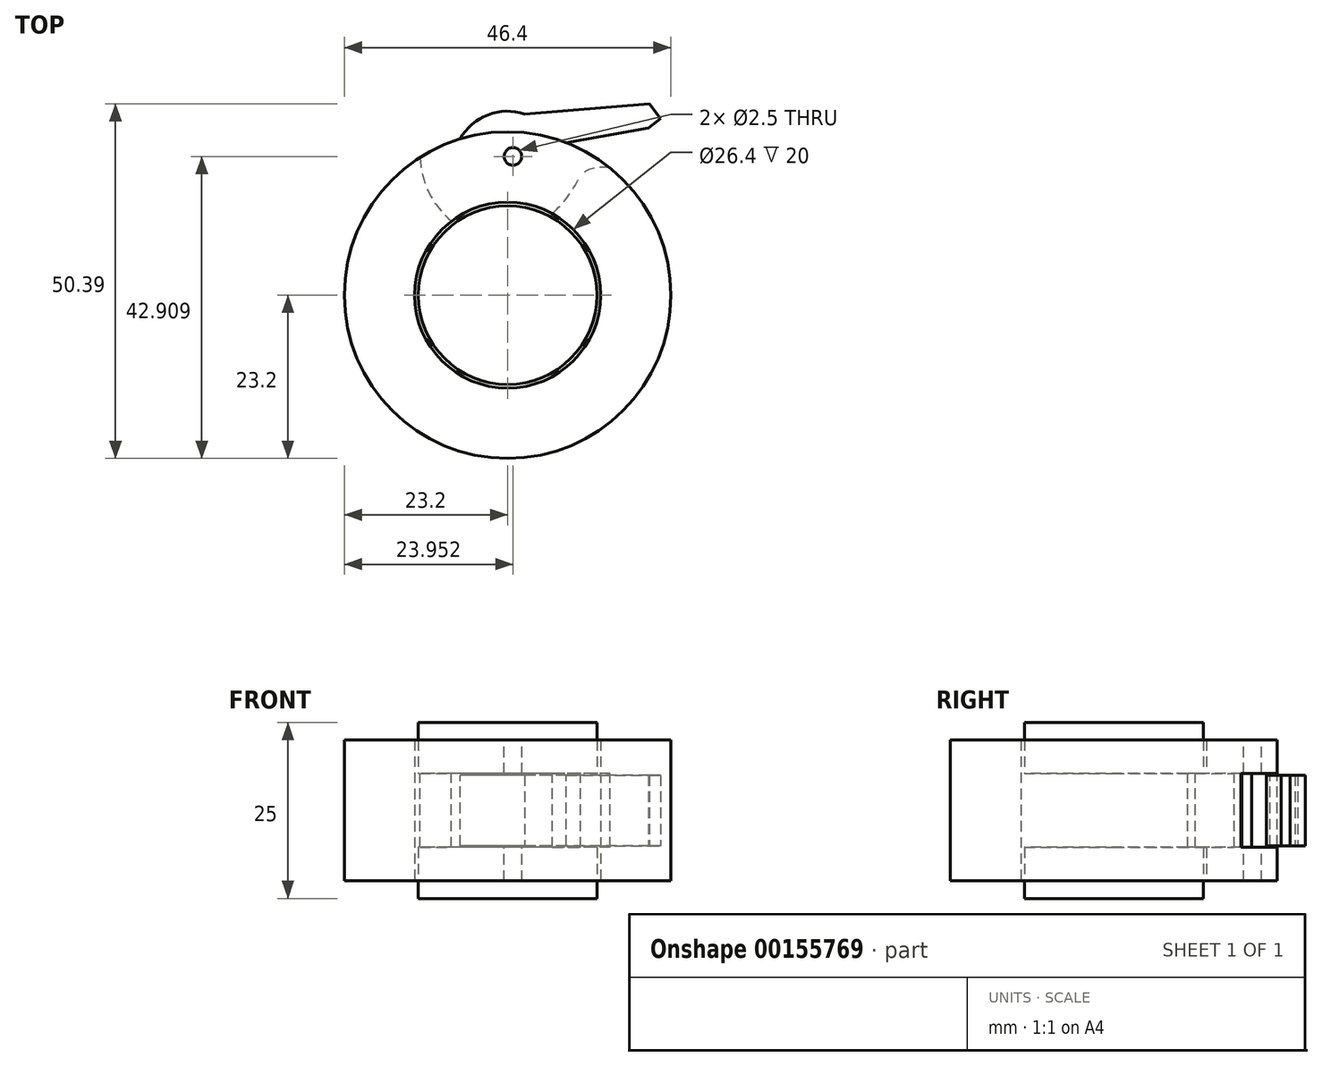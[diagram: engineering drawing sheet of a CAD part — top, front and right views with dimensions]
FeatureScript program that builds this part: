
annotation { "Feature Type Name" : "Feature", "Feature Type Description" : "" }
export const myFeature = defineFeature(function(context is Context, id is Id, definition is map)
    precondition{}
    {
        {
            var Q0;
            Q0=qCreatedBy(makeId("Top.planeOp"),FACE);
            var sketch = newSketch(context, id + "F0", { "sketchPlane" : qUnion([Q0])});
            skCircle(sketch, "E0", {"center": v(0, 0) * mm, "radius": 12.7 * mm});
            skSolve(sketch);
        }
        {
            var Q0;
            Q0 = qSketchRegion(id + "F0", true);
            extrude(context, id + "F1", {"entities" : qUnion([Q0]), "endBound" : BoundingType.SYMMETRIC, "depth" : 25 * mm, "offsetDistance" : 25 * mm});
        }
        {
            var Q0;
            Q0=qCreatedBy(makeId("Top.planeOp"),FACE);
            var sketch = newSketch(context, id + "F2", { "sketchPlane" : qUnion([Q0])});
            skCircle(sketch, "E1", {"center": v(0, 0) * mm, "radius": 13.2 * mm});
            skCircle(sketch, "E2", {"center": v(0, 0) * mm, "radius": 23.2 * mm});
            skSolve(sketch);
        }
        {
            var Q0;
            Q0 = qSketchRegion(id + "F2", true);
            extrude(context, id + "F3", {"entities" : qUnion([Q0]), "endBound" : BoundingType.SYMMETRIC, "depth" : 20 * mm, "offsetDistance" : 25 * mm});
        }
        {
            var Q0;
            Q0=qCreatedBy(makeId("Top.planeOp"),FACE);
            var sketch = newSketch(context, id + "F4", { "sketchPlane" : qUnion([Q0])});
            skCircle(sketch, "E3", {"center": v(0, 18.37) * mm, "radius": 7.76 * mm});
            skLineSegment(sketch, "E4", {"start": v(7.13, 21.43) * mm, "end": v(20, 23.77) * mm});
            skLineSegment(sketch, "E5", {"start": v(20, 23.77) * mm, "end": v(21.71, 25.06) * mm});
            skLineSegment(sketch, "E6", {"start": v(21.71, 25.06) * mm, "end": v(20.1, 27.19) * mm});
            skLineSegment(sketch, "E7", {"start": v(20.1, 27.19) * mm, "end": v(2.42, 25.75) * mm});
            skSolve(sketch);
        }
        {
            var Q0;
            Q0 = qSketchRegion(id + "F4", true);
            extrude(context, id + "F5", {"entities" : qUnion([Q0]), "endBound" : BoundingType.SYMMETRIC, "depth" : 10 * mm, "offsetDistance" : 25 * mm});
        }
        {
            var Q0;
            Q0=qCreatedBy(makeId("Top.planeOp"),FACE);
            var sketch = newSketch(context, id + "F6", { "sketchPlane" : qUnion([Q0])});
            skCircle(sketch, "E8", {"center": v(0.75, 19.7) * mm, "radius": 1.25 * mm});
            skSolve(sketch);
        }
        {
            var Q0;
            Q0 = qSketchRegion(id + "F6", true);
            extrude(context, id + "F7", {"entities" : qUnion([Q0]), "operationType" : NewBodyOperationType.REMOVE, "endBound" : BoundingType.SYMMETRIC, "oppositeDirection" : true, "depth" : 25 * mm, "offsetDistance" : 25 * mm});
        }
        {
            var Q0;
            Q0=qCreatedBy(makeId("Top.planeOp"),FACE);
            var sketch = newSketch(context, id + "F8", { "sketchPlane" : qUnion([Q0])});
            skArc(sketch, "E9.0.0", {"start": v(11.49, 20.16) * mm, "mid": v(-0.56, 23.2) * mm, "end": v(-12.45, 19.58) * mm});
            skArc(sketch, "E10", {"start": v(-12.45, 19.58) * mm, "mid": v(-11.18, 14.57) * mm, "end": v(-7.97, 10.52) * mm});
            skArc(sketch, "E11", {"start": v(6.35, 11.57) * mm, "mid": v(8.63, 14.15) * mm, "end": v(10.38, 17.1) * mm});
            skCircle(sketch, "E12.0", {"center": v(0, 0) * mm, "radius": 13.2 * mm});
            skArc(sketch, "E13.0", {"start": v(14.57, 18.06) * mm, "mid": v(1.3, 23.16) * mm, "end": v(-12.45, 19.58) * mm});
            skArc(sketch, "E14", {"start": v(14.57, 18.06) * mm, "mid": v(12.36, 18.07) * mm, "end": v(10.38, 17.1) * mm});
            skSolve(sketch);
        }
        {
            var Q0;
            Q0 = qSketchRegion(id + "F8", true);
            extrude(context, id + "F9", {"entities" : qUnion([Q0]), "operationType" : NewBodyOperationType.REMOVE, "endBound" : BoundingType.SYMMETRIC, "oppositeDirection" : true, "depth" : 10.5 * mm, "offsetDistance" : 25 * mm});
        }
    });
